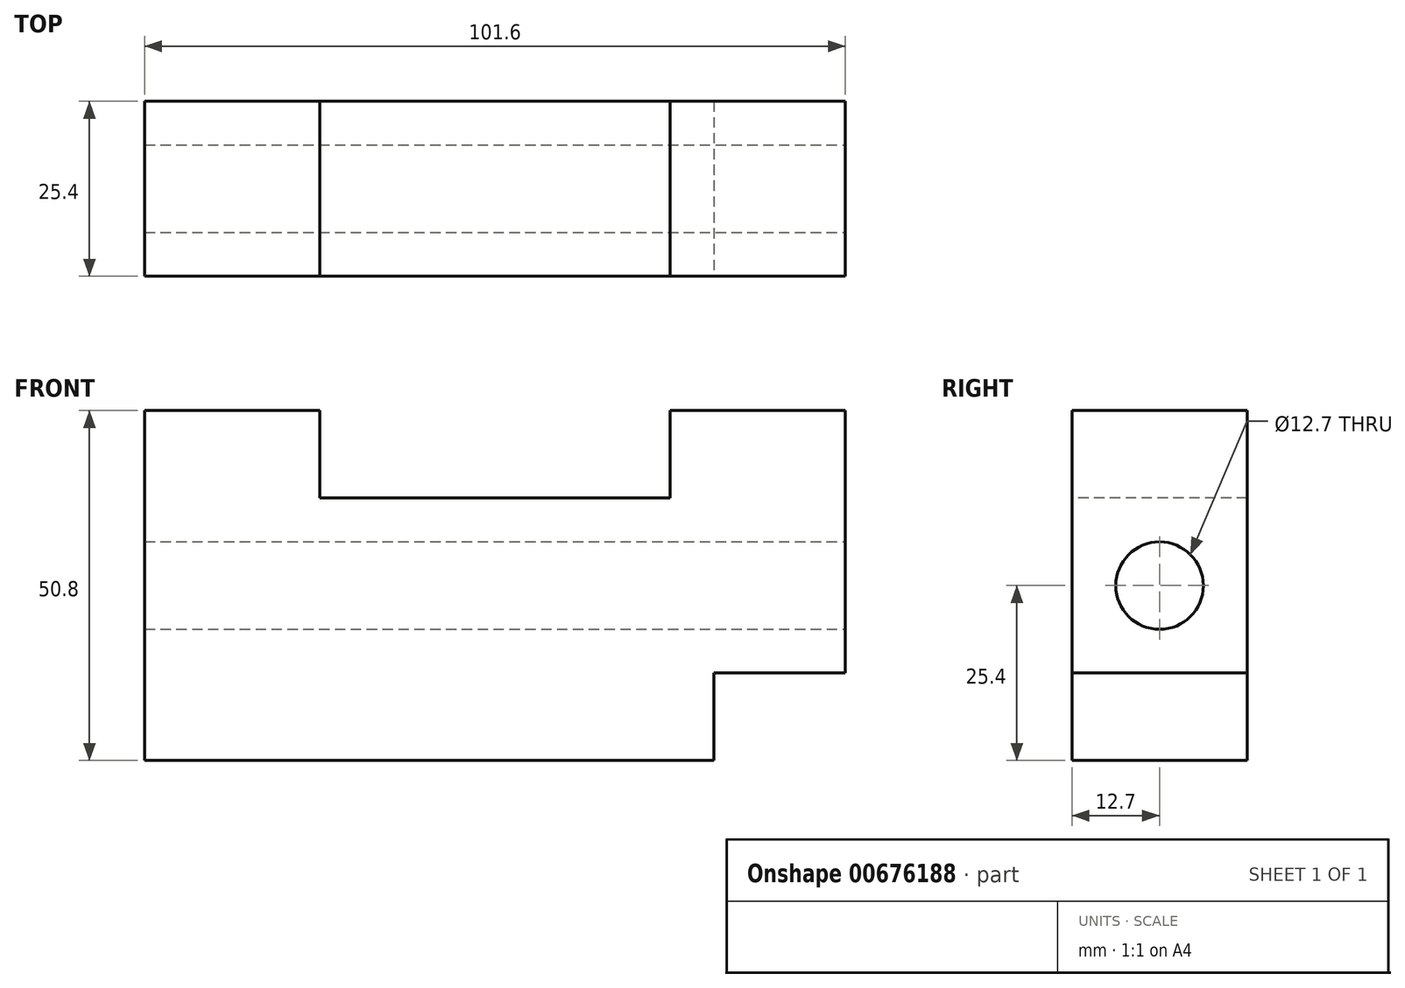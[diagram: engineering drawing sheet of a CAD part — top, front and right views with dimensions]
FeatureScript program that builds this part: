
annotation { "Feature Type Name" : "Feature", "Feature Type Description" : "" }
export const myFeature = defineFeature(function(context is Context, id is Id, definition is map)
    precondition{}
    {
        {
            var Q0;
            Q0=qCreatedBy(makeId("Front.planeOp"),FACE);
            var sketch = newSketch(context, id + "F0", { "sketchPlane" : qUnion([Q0])});
            skLineSegment(sketch, "E0.bottom", {"start": v(-50.8, 25.4) * mm, "end": v(50.8, 25.4) * mm});
            skLineSegment(sketch, "E0.top", {"start": v(-50.8, -25.4) * mm, "end": v(50.8, -25.4) * mm});
            skLineSegment(sketch, "E0.left", {"start": v(-50.8, 25.4) * mm, "end": v(-50.8, -25.4) * mm});
            skLineSegment(sketch, "E0.right", {"start": v(50.8, 25.4) * mm, "end": v(50.8, -25.4) * mm});
            skPoint(sketch, "E0.middle", {"position": v(0, 0) * mm});
            skLineSegment(sketch, "E1.bottom", {"start": v(50.8, -25.4) * mm, "end": v(31.75, -25.4) * mm});
            skLineSegment(sketch, "E1.top", {"start": v(50.8, -12.7) * mm, "end": v(31.75, -12.7) * mm});
            skLineSegment(sketch, "E1.left", {"start": v(50.8, -25.4) * mm, "end": v(50.8, -12.7) * mm});
            skLineSegment(sketch, "E1.right", {"start": v(31.75, -25.4) * mm, "end": v(31.75, -12.7) * mm});
            skSolve(sketch);
        }
        {
            var Q0;
            Q0 = qSketchRegion(id + "F0", true);
            extrude(context, id + "F1", {"entities" : qUnion([Q0]), "depth" : 25.4 * mm, "offsetDistance" : 25.4 * mm});
        }
        {
            var Q0;
            Q0=makeQuery(id+"F1.opExtrude","CAP_FACE",FACE,{"disambiguationData":[OSD([sQuery(id+"F0.wireOp",EDGE,"E0.bottom"),sQuery(id+"F0.wireOp",EDGE,"E0.top"),sQuery(id+"F0.wireOp",EDGE,"E0.left"),sQuery(id+"F0.wireOp",EDGE,"E0.right"),sQuery(id+"F0.wireOp",EDGE,"E1.bottom"),sQuery(id+"F0.wireOp",EDGE,"E1.left")])],"isStart":false});
            var sketch = newSketch(context, id + "F2", { "sketchPlane" : qUnion([Q0])});
            skLineSegment(sketch, "E2.bottom", {"start": v(50.8, -25.4) * mm, "end": v(31.75, -25.4) * mm});
            skLineSegment(sketch, "E2.top", {"start": v(50.8, -12.7) * mm, "end": v(31.75, -12.7) * mm});
            skLineSegment(sketch, "E2.left", {"start": v(50.8, -25.4) * mm, "end": v(50.8, -12.7) * mm});
            skLineSegment(sketch, "E2.right", {"start": v(31.75, -25.4) * mm, "end": v(31.75, -12.7) * mm});
            skSolve(sketch);
        }
        {
            var Q0;
            Q0 = qSketchRegion(id + "F2", true);
            extrude(context, id + "F3", {"entities" : qUnion([Q0]), "operationType" : NewBodyOperationType.REMOVE, "endBound" : BoundingType.THROUGH_ALL, "oppositeDirection" : true, "depth" : 25.4 * mm, "offsetDistance" : 25.4 * mm});
        }
        {
            var Q0;
            Q0=makeQuery(id+"F1.opExtrude","CAP_FACE",FACE,{"disambiguationData":[OSD([sQuery(id+"F0.wireOp",EDGE,"E0.bottom"),sQuery(id+"F0.wireOp",EDGE,"E0.top"),sQuery(id+"F0.wireOp",EDGE,"E0.left"),sQuery(id+"F0.wireOp",EDGE,"E0.right"),sQuery(id+"F0.wireOp",EDGE,"E1.bottom"),sQuery(id+"F0.wireOp",EDGE,"E1.left")])],"isStart":false});
            var sketch = newSketch(context, id + "F4", { "sketchPlane" : qUnion([Q0])});
            skLineSegment(sketch, "E3.bottom", {"start": v(-25.4, 25.4) * mm, "end": v(25.4, 25.4) * mm});
            skLineSegment(sketch, "E3.top", {"start": v(-25.4, 12.7) * mm, "end": v(25.4, 12.7) * mm});
            skLineSegment(sketch, "E3.left", {"start": v(-25.4, 25.4) * mm, "end": v(-25.4, 12.7) * mm});
            skLineSegment(sketch, "E3.right", {"start": v(25.4, 25.4) * mm, "end": v(25.4, 12.7) * mm});
            skPoint(sketch, "E3.middle", {"position": v(0, 19.05) * mm});
            skPoint(sketch, "E3.middle.positionSnap0", {"position": v(0, 25.4) * mm});
            skPoint(sketch, "E3.centerSnap0", {"position": v(0, 25.4) * mm});
            skSolve(sketch);
        }
        {
            var Q0;
            Q0 = qSketchRegion(id + "F4", true);
            extrude(context, id + "F5", {"entities" : qUnion([Q0]), "operationType" : NewBodyOperationType.REMOVE, "endBound" : BoundingType.THROUGH_ALL, "oppositeDirection" : true, "depth" : 25.4 * mm, "offsetDistance" : 25.4 * mm});
        }
        {
            var Q0;
            Q0=makeQuery(id+"F1.opExtrude","SWEPT_FACE",FACE,{"disambiguationData":[OSD([sQuery(id+"F0.wireOp",EDGE,"E0.right"),sQuery(id+"F0.wireOp",EDGE,"E1.left")])]});
            var sketch = newSketch(context, id + "F6", { "sketchPlane" : qUnion([Q0])});
            skCircle(sketch, "E4", {"center": v(-12.7, 0) * mm, "radius": 6.35 * mm});
            skSolve(sketch);
        }
        {
            var Q0;
            Q0=makeQuery(id+"F6.imprint","IMPRINT",FACE,{"disambiguationData":[TD([[makeQuery(id+"F6.imprint","IMPRINT",EDGE,{"derivedFrom":sQuery(id+"F6.wireOp",EDGE,"E4")}),1.0]])]});
            extrude(context, id + "F7", {"entities" : qUnion([Q0]), "operationType" : NewBodyOperationType.REMOVE, "endBound" : BoundingType.THROUGH_ALL, "depth" : 25.4 * mm, "offsetDistance" : 25.4 * mm});
        }
        {
            var Q0;
            Q0 = qSketchRegion(id + "F6", true);
            extrude(context, id + "F8", {"entities" : qUnion([Q0]), "operationType" : NewBodyOperationType.ADD, "depth" : 25.4 * mm, "offsetDistance" : 25.4 * mm});
        }
        {
            var Q0;
            Q0=makeQuery(id+"F8.opExtrude","CAP_FACE",FACE,{"disambiguationData":[OSD([sQuery(id+"F6.wireOp",EDGE,"E4")])],"isStart":false});
            extrude(context, id + "F9", {"entities" : qUnion([Q0]), "operationType" : NewBodyOperationType.REMOVE, "endBound" : BoundingType.THROUGH_ALL, "oppositeDirection" : true, "depth" : 101.6 * mm, "offsetDistance" : 25.4 * mm});
        }
    });
